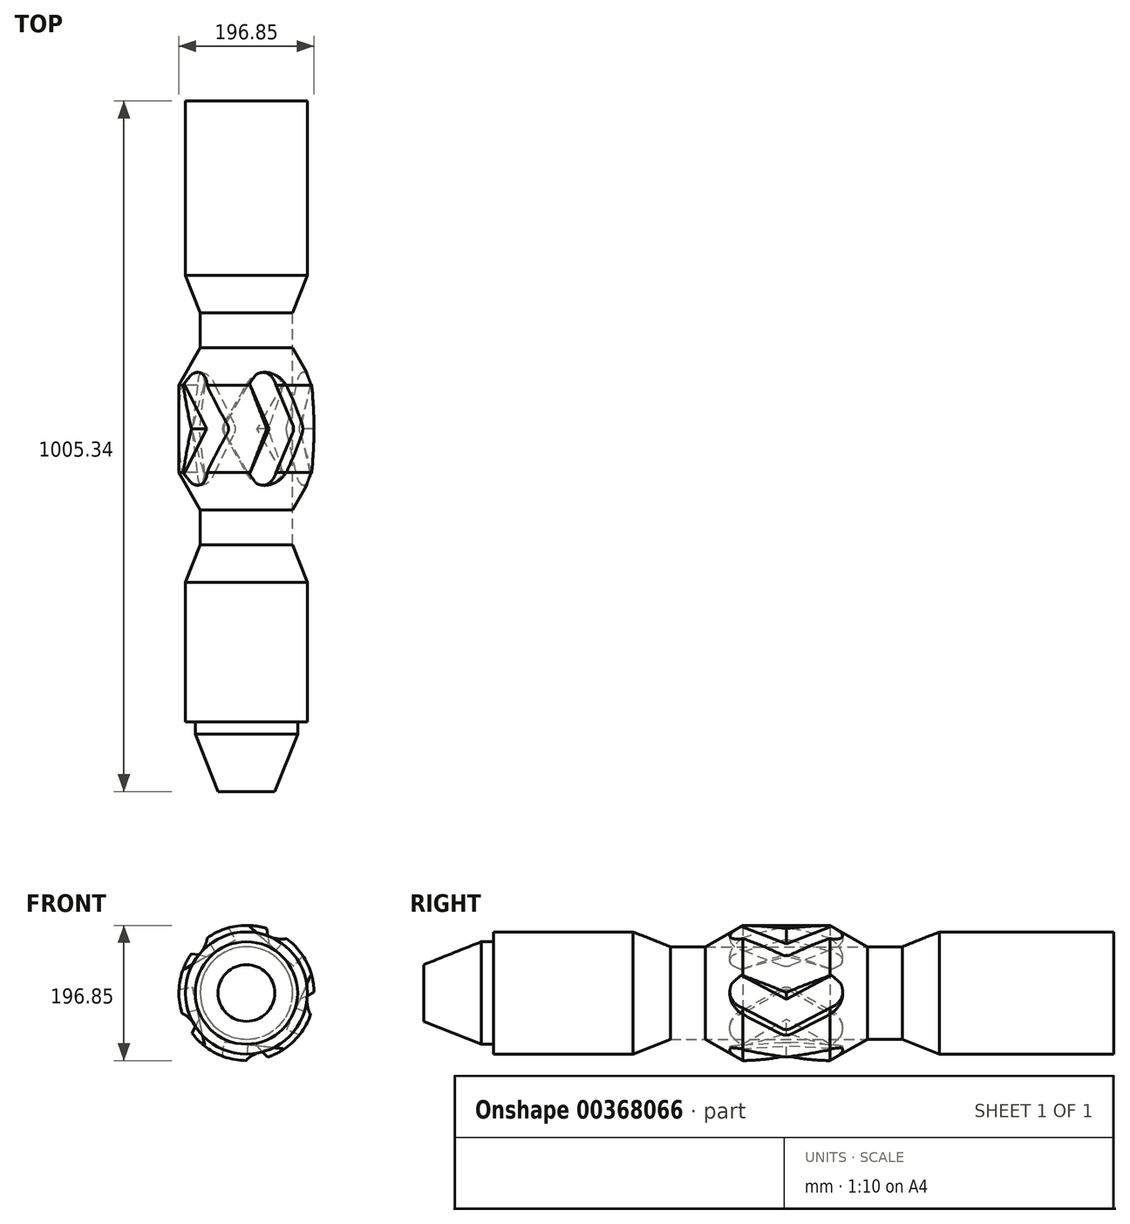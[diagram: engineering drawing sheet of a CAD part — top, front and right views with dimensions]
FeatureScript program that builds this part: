
annotation { "Feature Type Name" : "Feature", "Feature Type Description" : "" }
export const myFeature = defineFeature(function(context is Context, id is Id, definition is map)
    precondition{}
    {
        {
            var Q0;
            Q0=qCreatedBy(makeId("Right.planeOp"),FACE);
            var sketch = newSketch(context, id + "F0", { "sketchPlane" : qUnion([Q0])});
            skLineSegment(sketch, "E0", {"start": v(0, 0) * mm, "end": v(-54.48, 0) * mm});
            skLineSegment(sketch, "E1", {"start": v(-54.48, 0) * mm, "end": v(-54.48, 67.3) * mm});
            skLineSegment(sketch, "E2", {"start": v(0, 0) * mm, "end": v(63.5, 0) * mm});
            skLineSegment(sketch, "E3", {"start": v(63.5, 0) * mm, "end": v(63.5, 98.43) * mm});
            skLineSegment(sketch, "E4", {"start": v(-54.48, 67.3) * mm, "end": v(0, 98.42) * mm});
            skLineSegment(sketch, "E5", {"start": v(0, 98.42) * mm, "end": v(63.5, 98.43) * mm});
            skLineSegment(sketch, "E6", {"start": v(-54.48, 0) * mm, "end": v(-200.95, 0) * mm, "construction": true});
            skLineSegment(sketch, "E7", {"start": v(63.5, 0) * mm, "end": v(423.22, 0) * mm, "construction": true});
            skLineSegment(sketch, "E8", {"start": v(-200.95, 0) * mm, "end": v(-560.16, 0) * mm, "construction": true});
            skLineSegment(sketch, "E9", {"start": v(-54.48, 67.3) * mm, "end": v(-54.48, 155.07) * mm, "construction": true});
            skLineSegment(sketch, "E10", {"start": v(-54.48, 98.42) * mm, "end": v(-189.48, 98.42) * mm, "construction": true});
            skLineSegment(sketch, "E11", {"start": v(-54.48, 98.42) * mm, "end": v(207.19, 98.42) * mm, "construction": true});
            skPoint(sketch, "E11.endSnap0", {"position": v(31.75, 98.42) * mm});
            skLineSegment(sketch, "E12", {"start": v(-117.65, 67.3) * mm, "end": v(197.29, 67.3) * mm, "construction": true});
            skLineSegment(sketch, "E13", {"start": v(0, 67.3) * mm, "end": v(0, 159.28) * mm, "construction": true});
            skSolve(sketch);
        }
        {
            var Q0;
            Q0=qCreatedBy(makeId("Front.planeOp"),FACE);
            var sketch = newSketch(context, id + "F1", { "sketchPlane" : qUnion([Q0])});
            skCircle(sketch, "E14", {"center": v(0, 0) * mm, "radius": 98.42 * mm});
            skSolve(sketch);
        }
        {
            var Q0;
            Q0=sQuery(id+"F0.wireOp",EDGE,"E11");
            cPlane(context, id + "F2", {"entities" : qUnion([Q0]), "cplaneType" : CPlaneType.LINE_ANGLE, "offset" : 25.4 * mm, "angle" : 30 * degree, "oppositeDirection" : true, "width" : 152.4 * mm, "height" : 152.4 * mm});
        }
        {
            var Q0;
            Q0=qCreatedBy(id+"F2.planeOp",FACE);
            var sketch = newSketch(context, id + "F3", { "sketchPlane" : qUnion([Q0])});
            skLineSegment(sketch, "E15", {"start": v(-56.32, 6.52) * mm, "end": v(-16.06, 76.26) * mm});
            skLineSegment(sketch, "E16", {"start": v(-9.75, 0) * mm, "end": v(34.28, 76.26) * mm});
            skLineSegment(sketch, "E17", {"start": v(-16.06, 76.26) * mm, "end": v(34.28, 76.26) * mm});
            skPoint(sketch, "E18.third.point", {"position": v(-35.9, 30.56) * mm});
            skPoint(sketch, "E19.orphan", {"position": v(-91.05, -53.64) * mm});
            skPoint(sketch, "E20.third.point", {"position": v(-50.54, 32.5) * mm});
            skPoint(sketch, "E21.start.orphan", {"position": v(-40.72, -53.64) * mm});
            skPoint(sketch, "E22.third.point", {"position": v(-23.05, 38.58) * mm});
            skPoint(sketch, "E23.third.point", {"position": v(-42.04, 83.01) * mm});
            skPoint(sketch, "E24.third.point", {"position": v(-73.34, 33.72) * mm});
            skPoint(sketch, "E25.visualSharp", {"position": v(-65.3, -9.04) * mm});
            skPoint(sketch, "E26.second.point", {"position": v(-65.14, 27.43) * mm});
            skPoint(sketch, "E26.third.point", {"position": v(-62.66, -2.23) * mm});
            skPoint(sketch, "E26.third.point.positionSnap0", {"position": v(-61.37, -2.23) * mm});
            skPoint(sketch, "E27.orphan", {"position": v(-62.66, -4.46) * mm});
            skPoint(sketch, "E28.visualSharp", {"position": v(-61.96, -3.24) * mm});
            skPoint(sketch, "E29.second.point", {"position": v(-59.08, 19.07) * mm});
            skPoint(sketch, "E30.newPointB", {"position": v(-60.09, 0) * mm});
            skPoint(sketch, "E31.third.point", {"position": v(-34.42, 24.2) * mm});
            skPoint(sketch, "E32.third.point", {"position": v(-63.05, 18.73) * mm});
            skPoint(sketch, "E33.third.point", {"position": v(-54.33, 26.5) * mm});
            skLineSegment(sketch, "E34", {"start": v(-56.32, 6.52) * mm, "end": v(-61.37, -2.23) * mm});
            skPoint(sketch, "E35.third.point", {"position": v(-51.38, 8.57) * mm});
            skArc(sketch, "E36", {"start": v(-61.37, -2.23) * mm, "mid": v(-34.8, -18.78) * mm, "end": v(-9.75, 0) * mm});
            skSolve(sketch);
        }
        {
            var Q0;
            Q0=makeQuery(id+"F0.imprint","IMPRINT",FACE,{"disambiguationData":[TD([[makeQuery(id+"F0.imprint","IMPRINT",EDGE,{"derivedFrom":sQuery(id+"F0.wireOp",EDGE,"E0")}),-1.0]])]});
            var Q1;
            Q1=sQuery(id+"F0.wireOp",EDGE,"E2");
            revolve(context, id + "F4", {"entities" : qUnion([Q0]), "axis" : qUnion([Q1]), "revolveType" : RevolveType.FULL});
        }
        {
            var Q0;
            Q0=qSketchRegion(id+"F3",true);
            extrude(context, id + "F5", {"entities" : qUnion([Q0]), "oppositeDirection" : true, "depth" : 10.16 * mm, "hasSecondDirection" : true, "secondDirectionOppositeDirection" : false, "secondDirectionDepth" : 20.32 * mm});
        }
        {
            var Q0;
            Q0=makeQuery(id+"F5.opExtrude","SWEPT_BODY",BODY,{"disambiguationData":[OSD([sQuery(id+"F3.wireOp",EDGE,"E15"),sQuery(id+"F3.wireOp",EDGE,"E16"),sQuery(id+"F3.wireOp",EDGE,"E17"),sQuery(id+"F3.wireOp",EDGE,"E18")])]});
            var Q1;
            Q1=sQuery(id+"F1.wireOp",EDGE,"E14");
            circularPattern(context, id + "F6", {"entities" : qUnion([Q0]), "axis" : qUnion([Q1]), "angle" : 360 * degree, "instanceCount" : 5, "equalSpace" : true});
        }
        {
            var Q0;
            Q0=makeQuery(id+"F5.opExtrude","SWEPT_BODY",BODY,{"disambiguationData":[OSD([sQuery(id+"F3.wireOp",EDGE,"E15"),sQuery(id+"F3.wireOp",EDGE,"E16"),sQuery(id+"F3.wireOp",EDGE,"E17"),sQuery(id+"F3.wireOp",EDGE,"E18")])]});
            var Q1;
            Q1=makeQuery(id+"F6.opPattern","COPY",BODY,{"derivedFrom":makeQuery(id+"F5.opExtrude","SWEPT_BODY",BODY,{"disambiguationData":[OSD([sQuery(id+"F3.wireOp",EDGE,"E15"),sQuery(id+"F3.wireOp",EDGE,"E16"),sQuery(id+"F3.wireOp",EDGE,"E17"),sQuery(id+"F3.wireOp",EDGE,"E18")])]}),"instanceName":"4"});
            var Q2;
            Q2=makeQuery(id+"F6.opPattern","COPY",BODY,{"derivedFrom":makeQuery(id+"F5.opExtrude","SWEPT_BODY",BODY,{"disambiguationData":[OSD([sQuery(id+"F3.wireOp",EDGE,"E15"),sQuery(id+"F3.wireOp",EDGE,"E16"),sQuery(id+"F3.wireOp",EDGE,"E17"),sQuery(id+"F3.wireOp",EDGE,"E18")])]}),"instanceName":"3"});
            var Q3;
            Q3=makeQuery(id+"F6.opPattern","COPY",BODY,{"derivedFrom":makeQuery(id+"F5.opExtrude","SWEPT_BODY",BODY,{"disambiguationData":[OSD([sQuery(id+"F3.wireOp",EDGE,"E15"),sQuery(id+"F3.wireOp",EDGE,"E16"),sQuery(id+"F3.wireOp",EDGE,"E17"),sQuery(id+"F3.wireOp",EDGE,"E18")])]}),"instanceName":"1"});
            var Q4;
            Q4=makeQuery(id+"F6.opPattern","COPY",BODY,{"derivedFrom":makeQuery(id+"F5.opExtrude","SWEPT_BODY",BODY,{"disambiguationData":[OSD([sQuery(id+"F3.wireOp",EDGE,"E15"),sQuery(id+"F3.wireOp",EDGE,"E16"),sQuery(id+"F3.wireOp",EDGE,"E17"),sQuery(id+"F3.wireOp",EDGE,"E18")])]}),"instanceName":"2"});
            var Q5;
            Q5=makeQuery(id+"F4.opRevolve","SWEPT_BODY",BODY,{"disambiguationData":[OSD([sQuery(id+"F0.wireOp",EDGE,"E0"),sQuery(id+"F0.wireOp",EDGE,"E1"),sQuery(id+"F0.wireOp",EDGE,"E2"),sQuery(id+"F0.wireOp",EDGE,"E3"),sQuery(id+"F0.wireOp",EDGE,"E4"),sQuery(id+"F0.wireOp",EDGE,"E5")])]});
            booleanBodies(context, id + "F7", {"operationType" : BooleanOperationType.SUBTRACTION, "tools" : qUnion([Q0, Q1, Q2, Q3, Q4]), "targets" : qUnion([Q5])});
        }
        {
            var Q0;
            Q0=makeQuery(id+"F7.opBoolean","INTERSECT",EDGE,{"derivedFrom":[makeQuery(id+"F4.opRevolve","SWEPT_FACE",FACE,{"disambiguationData":[OSD([sQuery(id+"F0.wireOp",EDGE,"E3")])]}),makeQuery(id+"F6.opPattern","COPY",FACE,{"derivedFrom":makeQuery(id+"F5.opExtrude","SWEPT_FACE",FACE,{"disambiguationData":[OSD([sQuery(id+"F3.wireOp",EDGE,"E15")])]}),"instanceName":"4"})]});
            cPlane(context, id + "F8", {"entities" : qUnion([Q0]), "cplaneType" : CPlaneType.LINE_ANGLE, "offset" : 25.4 * mm, "angle" : 60 * degree, "width" : 152.4 * mm, "height" : 152.4 * mm});
        }
        {
            var Q0;
            Q0=qCreatedBy(id+"F8.planeOp",FACE);
            var sketch = newSketch(context, id + "F9", { "sketchPlane" : qUnion([Q0])});
            skLineSegment(sketch, "E37", {"start": v(-18.07, 89.52) * mm, "end": v(-18.07, 89.65) * mm});
            skLineSegment(sketch, "E38", {"start": v(-18.07, 89.65) * mm, "end": v(-18.07, 111.81) * mm});
            skArc(sketch, "E39", {"start": v(-18.07, 111.81) * mm, "mid": v(-29.54, 108.63) * mm, "end": v(-37.74, 100) * mm});
            skLineSegment(sketch, "E40", {"start": v(-18.07, 89.52) * mm, "end": v(-37.74, 100) * mm});
            skSolve(sketch);
        }
        {
            var Q0;
            Q0 = qSketchRegion(id + "F9", true);
            var Q1;
            Q1=makeQuery(id+"F7.opBoolean","COPY",FACE,{"derivedFrom":makeQuery(id+"F6.opPattern","COPY",FACE,{"derivedFrom":makeQuery(id+"F5.opExtrude","SWEPT_FACE",FACE,{"disambiguationData":[OSD([sQuery(id+"F3.wireOp",EDGE,"E20")])]}),"instanceName":"4"})});
            var Q2;
            Q2=makeQuery(id+"F4.opRevolve","SWEPT_BODY",BODY,{"disambiguationData":[OSD([sQuery(id+"F0.wireOp",EDGE,"E0"),sQuery(id+"F0.wireOp",EDGE,"E1"),sQuery(id+"F0.wireOp",EDGE,"E2"),sQuery(id+"F0.wireOp",EDGE,"E3"),sQuery(id+"F0.wireOp",EDGE,"E4"),sQuery(id+"F0.wireOp",EDGE,"E5")])]});
            var Q3;
            Q3=makeQuery(id+"F7.opBoolean","INTERSECT",VERTEX,{"derivedFrom":[makeQuery(id+"F4.opRevolve","SWEPT_FACE",FACE,{"disambiguationData":[OSD([sQuery(id+"F0.wireOp",EDGE,"E4")])]}),makeQuery(id+"F4.opRevolve","SWEPT_FACE",FACE,{"disambiguationData":[OSD([sQuery(id+"F0.wireOp",EDGE,"E5")])]}),makeQuery(id+"F6.opPattern","COPY",FACE,{"derivedFrom":makeQuery(id+"F5.opExtrude","SWEPT_FACE",FACE,{"disambiguationData":[OSD([sQuery(id+"F3.wireOp",EDGE,"E15")])]}),"instanceName":"4"}),makeQuery(id+"F6.opPattern","COPY",FACE,{"derivedFrom":makeQuery(id+"F5.opExtrude","SWEPT_FACE",FACE,{"disambiguationData":[OSD([sQuery(id+"F3.wireOp",EDGE,"E20")])]}),"instanceName":"4"})]});
            extrude(context, id + "F10", {"entities" : qUnion([Q0]), "oppositeDirection" : true, "endBoundEntityFace" : qUnion([Q1]), "endBoundEntityBody" : qUnion([Q2]), "endBoundEntityVertex" : qUnion([Q3]), "depth" : 78.23 * mm});
        }
        {
            var Q0;
            Q0=makeQuery(id+"F10.opExtrude","SWEPT_BODY",BODY,{"disambiguationData":[OSD([sQuery(id+"F9.wireOp",EDGE,"E37"),sQuery(id+"F9.wireOp",EDGE,"E38"),sQuery(id+"F9.wireOp",EDGE,"E39"),sQuery(id+"F9.wireOp",EDGE,"E40")])]});
            var Q1;
            Q1=makeQuery(id+"F7.opBoolean","SPLIT",FACE,{"disambiguationData":[TD([makeQuery(id+"F5.opExtrude","SWEPT_FACE",FACE,{"disambiguationData":[OSD([sQuery(id+"F3.wireOp",EDGE,"E16")])]})])],"derivedFrom":makeQuery(id+"F4.opRevolve","SWEPT_FACE",FACE,{"disambiguationData":[OSD([sQuery(id+"F0.wireOp",EDGE,"E5")])]})});
            circularPattern(context, id + "F11", {"entities" : qUnion([Q0]), "axis" : qUnion([Q1]), "angle" : 360 * degree, "instanceCount" : 5, "equalSpace" : true});
        }
        {
            var Q0;
            Q0=makeQuery(id+"F10.opExtrude","SWEPT_BODY",BODY,{"disambiguationData":[OSD([sQuery(id+"F9.wireOp",EDGE,"E37"),sQuery(id+"F9.wireOp",EDGE,"E38"),sQuery(id+"F9.wireOp",EDGE,"E39"),sQuery(id+"F9.wireOp",EDGE,"E40")])]});
            var Q1;
            Q1=makeQuery(id+"F11.opPattern","COPY",BODY,{"derivedFrom":makeQuery(id+"F10.opExtrude","SWEPT_BODY",BODY,{"disambiguationData":[OSD([sQuery(id+"F9.wireOp",EDGE,"E37"),sQuery(id+"F9.wireOp",EDGE,"E38"),sQuery(id+"F9.wireOp",EDGE,"E39"),sQuery(id+"F9.wireOp",EDGE,"E40")])]}),"instanceName":"1"});
            var Q2;
            Q2=makeQuery(id+"F11.opPattern","COPY",BODY,{"derivedFrom":makeQuery(id+"F10.opExtrude","SWEPT_BODY",BODY,{"disambiguationData":[OSD([sQuery(id+"F9.wireOp",EDGE,"E37"),sQuery(id+"F9.wireOp",EDGE,"E38"),sQuery(id+"F9.wireOp",EDGE,"E39"),sQuery(id+"F9.wireOp",EDGE,"E40")])]}),"instanceName":"2"});
            var Q3;
            Q3=makeQuery(id+"F11.opPattern","COPY",BODY,{"derivedFrom":makeQuery(id+"F10.opExtrude","SWEPT_BODY",BODY,{"disambiguationData":[OSD([sQuery(id+"F9.wireOp",EDGE,"E37"),sQuery(id+"F9.wireOp",EDGE,"E38"),sQuery(id+"F9.wireOp",EDGE,"E39"),sQuery(id+"F9.wireOp",EDGE,"E40")])]}),"instanceName":"3"});
            var Q4;
            Q4=makeQuery(id+"F11.opPattern","COPY",BODY,{"derivedFrom":makeQuery(id+"F10.opExtrude","SWEPT_BODY",BODY,{"disambiguationData":[OSD([sQuery(id+"F9.wireOp",EDGE,"E37"),sQuery(id+"F9.wireOp",EDGE,"E38"),sQuery(id+"F9.wireOp",EDGE,"E39"),sQuery(id+"F9.wireOp",EDGE,"E40")])]}),"instanceName":"4"});
            var Q5;
            Q5=makeQuery(id+"F4.opRevolve","SWEPT_BODY",BODY,{"disambiguationData":[OSD([sQuery(id+"F0.wireOp",EDGE,"E0"),sQuery(id+"F0.wireOp",EDGE,"E1"),sQuery(id+"F0.wireOp",EDGE,"E2"),sQuery(id+"F0.wireOp",EDGE,"E3"),sQuery(id+"F0.wireOp",EDGE,"E4"),sQuery(id+"F0.wireOp",EDGE,"E5")])]});
            booleanBodies(context, id + "F12", {"operationType" : BooleanOperationType.SUBTRACTION, "tools" : qUnion([Q0, Q1, Q2, Q3, Q4]), "targets" : qUnion([Q5])});
        }
        {
            var Q0;
            Q0=makeQuery(id+"F4.opRevolve","SWEPT_BODY",BODY,{"disambiguationData":[OSD([sQuery(id+"F0.wireOp",EDGE,"E0"),sQuery(id+"F0.wireOp",EDGE,"E1"),sQuery(id+"F0.wireOp",EDGE,"E2"),sQuery(id+"F0.wireOp",EDGE,"E3"),sQuery(id+"F0.wireOp",EDGE,"E4"),sQuery(id+"F0.wireOp",EDGE,"E5")])]});
            var Q1;
            Q1=makeQuery(id+"F4.opRevolve","SWEPT_FACE",FACE,{"disambiguationData":[OSD([sQuery(id+"F0.wireOp",EDGE,"E3")])]});
            mirror(context, id + "F13", {"operationType" : NewBodyOperationType.ADD, "entities" : qUnion([Q0]), "mirrorPlane" : qUnion([Q1])});
        }
        {
            var Q0;
            {var subQ0=makeQuery(id+"F7.opBoolean","INTERSECT",EDGE,{"derivedFrom":[makeQuery(id+"F4.opRevolve","SWEPT_FACE",FACE,{"disambiguationData":[OSD([sQuery(id+"F0.wireOp",EDGE,"E3")])]}),makeQuery(id+"F6.opPattern","COPY",FACE,{"derivedFrom":makeQuery(id+"F5.opExtrude","SWEPT_FACE",FACE,{"disambiguationData":[OSD([sQuery(id+"F3.wireOp",EDGE,"E16")])]}),"instanceName":"3"})]});Q0=makeQuery(id+"F13.boolean.opBoolean","MERGE",EDGE,{"derivedFrom":[subQ0,makeQuery(id+"F13.opPattern","COPY",EDGE,{"derivedFrom":subQ0,"instanceName":"1"})]});}
            var Q1;
            {var subQ0=makeQuery(id+"F7.opBoolean","INTERSECT",EDGE,{"derivedFrom":[makeQuery(id+"F4.opRevolve","SWEPT_FACE",FACE,{"disambiguationData":[OSD([sQuery(id+"F0.wireOp",EDGE,"E3")])]}),makeQuery(id+"F6.opPattern","COPY",FACE,{"derivedFrom":makeQuery(id+"F5.opExtrude","SWEPT_FACE",FACE,{"disambiguationData":[OSD([sQuery(id+"F3.wireOp",EDGE,"E16")])]}),"instanceName":"2"})]});Q1=makeQuery(id+"F13.boolean.opBoolean","MERGE",EDGE,{"derivedFrom":[subQ0,makeQuery(id+"F13.opPattern","COPY",EDGE,{"derivedFrom":subQ0,"instanceName":"1"})]});}
            var Q2;
            {var subQ0=makeQuery(id+"F7.opBoolean","INTERSECT",EDGE,{"derivedFrom":[makeQuery(id+"F4.opRevolve","SWEPT_FACE",FACE,{"disambiguationData":[OSD([sQuery(id+"F0.wireOp",EDGE,"E3")])]}),makeQuery(id+"F6.opPattern","COPY",FACE,{"derivedFrom":makeQuery(id+"F5.opExtrude","SWEPT_FACE",FACE,{"disambiguationData":[OSD([sQuery(id+"F3.wireOp",EDGE,"E16")])]}),"instanceName":"1"})]});Q2=makeQuery(id+"F13.boolean.opBoolean","MERGE",EDGE,{"derivedFrom":[subQ0,makeQuery(id+"F13.opPattern","COPY",EDGE,{"derivedFrom":subQ0,"instanceName":"1"})]});}
            var Q3;
            {var subQ0=makeQuery(id+"F7.opBoolean","INTERSECT",EDGE,{"derivedFrom":[makeQuery(id+"F4.opRevolve","SWEPT_FACE",FACE,{"disambiguationData":[OSD([sQuery(id+"F0.wireOp",EDGE,"E3")])]}),makeQuery(id+"F5.opExtrude","SWEPT_FACE",FACE,{"disambiguationData":[OSD([sQuery(id+"F3.wireOp",EDGE,"E16")])]})]});Q3=makeQuery(id+"F13.boolean.opBoolean","MERGE",EDGE,{"derivedFrom":[subQ0,makeQuery(id+"F13.opPattern","COPY",EDGE,{"derivedFrom":subQ0,"instanceName":"1"})]});}
            var Q4;
            {var subQ0=makeQuery(id+"F7.opBoolean","INTERSECT",EDGE,{"derivedFrom":[makeQuery(id+"F4.opRevolve","SWEPT_FACE",FACE,{"disambiguationData":[OSD([sQuery(id+"F0.wireOp",EDGE,"E3")])]}),makeQuery(id+"F6.opPattern","COPY",FACE,{"derivedFrom":makeQuery(id+"F5.opExtrude","SWEPT_FACE",FACE,{"disambiguationData":[OSD([sQuery(id+"F3.wireOp",EDGE,"E16")])]}),"instanceName":"4"})]});Q4=makeQuery(id+"F13.boolean.opBoolean","MERGE",EDGE,{"derivedFrom":[subQ0,makeQuery(id+"F13.opPattern","COPY",EDGE,{"derivedFrom":subQ0,"instanceName":"1"})]});}
            fillet(context, id + "F14", {"entities" : qUnion([Q0, Q1, Q2, Q3, Q4]), "radius" : 12.7 * mm, "tangentPropagation" : true, "allowEdgeOverflow" : false});
        }
        {
            var Q0;
            Q0=qCreatedBy(makeId("Right.planeOp"),FACE);
            var sketch = newSketch(context, id + "F15", { "sketchPlane" : qUnion([Q0])});
            skLineSegment(sketch, "E41", {"start": v(0, 0) * mm, "end": v(-54.48, 0) * mm});
            skLineSegment(sketch, "E42", {"start": v(-54.48, 0) * mm, "end": v(-105.28, 0) * mm});
            skLineSegment(sketch, "E43", {"start": v(-105.28, 0) * mm, "end": v(-159.77, 0) * mm});
            skLineSegment(sketch, "E44", {"start": v(0, 0) * mm, "end": v(181.48, 0) * mm});
            skLineSegment(sketch, "E45", {"start": v(181.48, 0) * mm, "end": v(232.28, 0) * mm});
            skLineSegment(sketch, "E46", {"start": v(232.28, 0) * mm, "end": v(286.77, 0) * mm});
            skPoint(sketch, "E46.endSnap0", {"position": v(90.74, 0) * mm});
            skLineSegment(sketch, "E47", {"start": v(286.77, 0) * mm, "end": v(540.77, 0) * mm});
            skLineSegment(sketch, "E48", {"start": v(540.77, 0) * mm, "end": v(540.77, 88.9) * mm});
            skLineSegment(sketch, "E49", {"start": v(286.77, 0) * mm, "end": v(286.77, 88.9) * mm});
            skLineSegment(sketch, "E50", {"start": v(181.48, 0) * mm, "end": v(181.48, 67.31) * mm});
            skLineSegment(sketch, "E51", {"start": v(232.28, 0) * mm, "end": v(232.28, 67.31) * mm});
            skLineSegment(sketch, "E52", {"start": v(-54.48, 0) * mm, "end": v(-54.48, 67.31) * mm});
            skLineSegment(sketch, "E53", {"start": v(-159.77, 0) * mm, "end": v(-362.97, 0) * mm});
            skLineSegment(sketch, "E54", {"start": v(-362.97, 0) * mm, "end": v(-464.57, 0) * mm});
            skLineSegment(sketch, "E55", {"start": v(-105.28, 0) * mm, "end": v(-105.28, 67.3) * mm});
            skLineSegment(sketch, "E56", {"start": v(-159.77, 0) * mm, "end": v(-159.77, 88.9) * mm});
            skLineSegment(sketch, "E57", {"start": v(-362.97, 0) * mm, "end": v(-362.97, 88.9) * mm});
            skLineSegment(sketch, "E58", {"start": v(-464.57, 0) * mm, "end": v(-464.57, 41.27) * mm});
            skLineSegment(sketch, "E59", {"start": v(-362.97, 88.9) * mm, "end": v(-159.77, 88.9) * mm});
            skLineSegment(sketch, "E60", {"start": v(-159.77, 88.9) * mm, "end": v(-105.28, 67.3) * mm});
            skLineSegment(sketch, "E61", {"start": v(-105.28, 67.3) * mm, "end": v(-54.48, 67.31) * mm});
            skLineSegment(sketch, "E62", {"start": v(181.48, 67.31) * mm, "end": v(-54.48, 67.31) * mm});
            skLineSegment(sketch, "E63", {"start": v(181.48, 67.31) * mm, "end": v(232.28, 67.31) * mm});
            skLineSegment(sketch, "E64", {"start": v(232.28, 67.3) * mm, "end": v(286.77, 88.9) * mm});
            skLineSegment(sketch, "E65", {"start": v(286.77, 88.9) * mm, "end": v(540.77, 88.9) * mm});
            skLineSegment(sketch, "E66", {"start": v(-362.97, 74.55) * mm, "end": v(-381.03, 74.55) * mm});
            skLineSegment(sketch, "E67", {"start": v(-381.03, 74.55) * mm, "end": v(-464.57, 41.27) * mm});
            skSolve(sketch);
        }
        {
            var Q0;
            Q0 = qSketchRegion(id + "F15", true);
            var Q1;
            Q1=sQuery(id+"F15.wireOp",EDGE,"E53");
            revolve(context, id + "F16", {"entities" : qUnion([Q0]), "axis" : qUnion([Q1]), "revolveType" : RevolveType.FULL});
        }
    });
